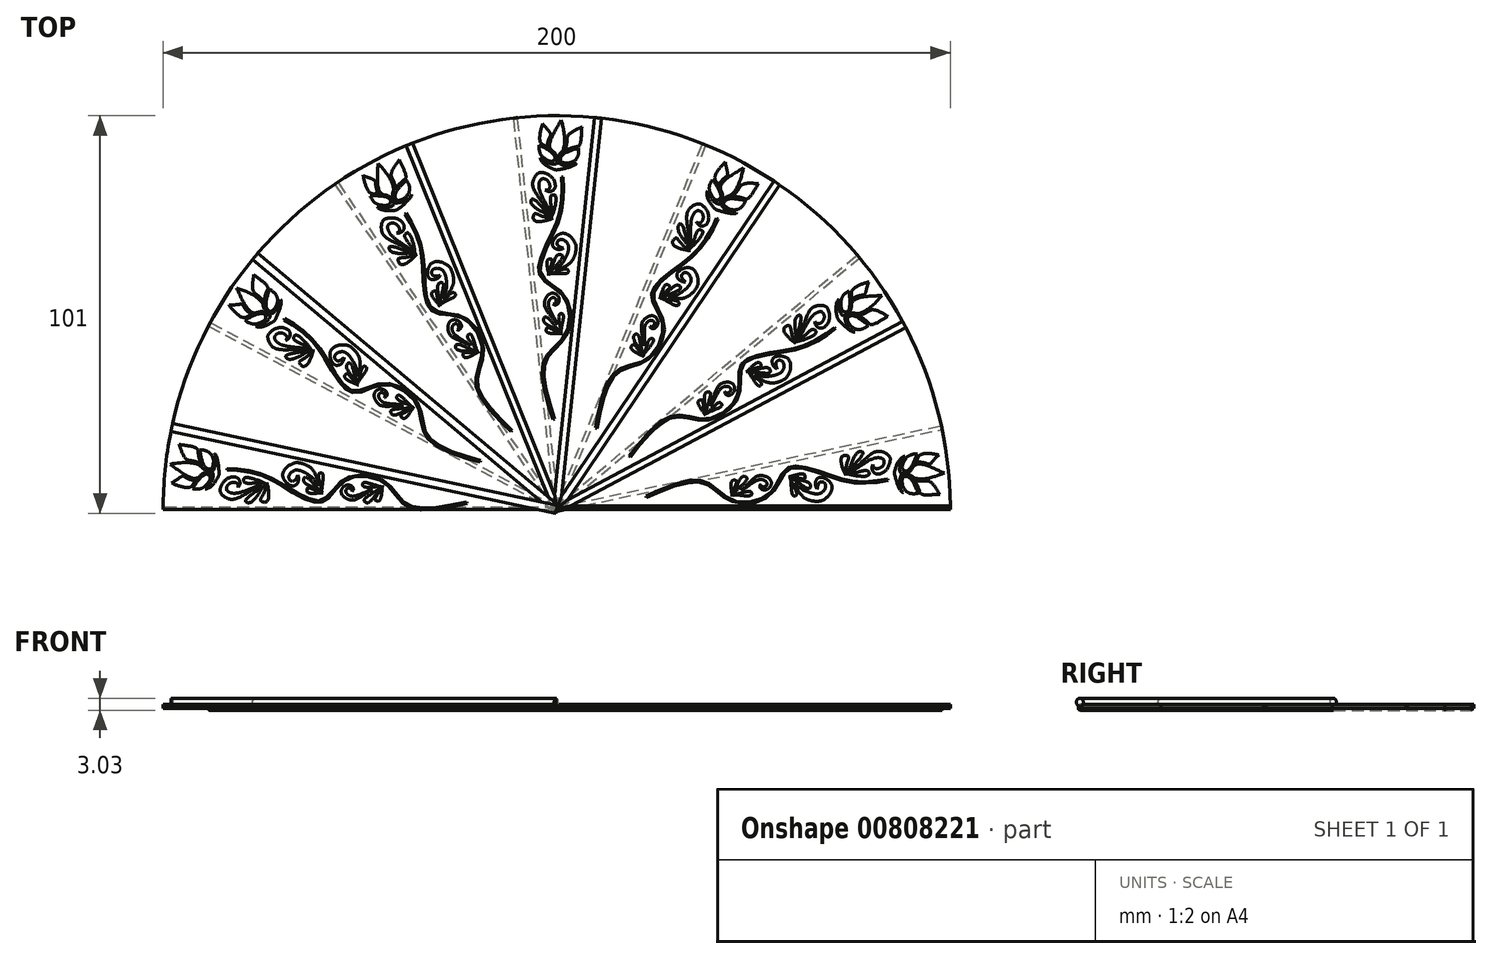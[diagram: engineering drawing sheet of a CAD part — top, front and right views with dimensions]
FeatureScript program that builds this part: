
annotation { "Feature Type Name" : "Feature", "Feature Type Description" : "" }
export const myFeature = defineFeature(function(context is Context, id is Id, definition is map)
    precondition{}
    {
        {
            var Q0;
            Q0=qCreatedBy(makeId("Top.planeOp"),FACE);
            var sketch = newSketch(context, id + "F0", { "sketchPlane" : qUnion([Q0])});
            skLineSegment(sketch, "E0", {"start": v(0, 0) * mm, "end": v(100, 0) * mm});
            skLineSegment(sketch, "E1", {"start": v(0, 0) * mm, "end": v(-100, 0) * mm});
            skArc(sketch, "E2", {"start": v(100, 0) * mm, "mid": v(0, 100) * mm, "end": v(-100, 0) * mm});
            skLineSegment(sketch, "E3.1.0", {"start": v(0, 0) * mm, "end": v(-97.5, 22.25) * mm});
            skLineSegment(sketch, "E3.2.0", {"start": v(0, 0) * mm, "end": v(-90.1, 43.39) * mm});
            skLineSegment(sketch, "E3.3.0", {"start": v(0, 0) * mm, "end": v(-78.18, 62.35) * mm});
            skLineSegment(sketch, "E3.4.0", {"start": v(0, 0) * mm, "end": v(-62.35, 78.18) * mm});
            skLineSegment(sketch, "E3.5.0", {"start": v(0, 0) * mm, "end": v(-43.39, 90.1) * mm});
            skLineSegment(sketch, "E3.6.0", {"start": v(0, 0) * mm, "end": v(-22.25, 97.5) * mm});
            skLineSegment(sketch, "E3.7.0", {"start": v(0, 0) * mm, "end": v(0, 100) * mm});
            skLineSegment(sketch, "E3.8.0", {"start": v(0, 0) * mm, "end": v(22.25, 97.5) * mm});
            skLineSegment(sketch, "E3.9.0", {"start": v(0, 0) * mm, "end": v(43.39, 90.1) * mm});
            skLineSegment(sketch, "E3.10.0", {"start": v(0, 0) * mm, "end": v(62.35, 78.18) * mm});
            skLineSegment(sketch, "E3.11.0", {"start": v(0, 0) * mm, "end": v(78.18, 62.35) * mm});
            skLineSegment(sketch, "E3.12.0", {"start": v(0, 0) * mm, "end": v(90.1, 43.39) * mm});
            skLineSegment(sketch, "E3.13.0", {"start": v(0, 0) * mm, "end": v(97.5, 22.25) * mm});
            skLineSegment(sketch, "E3.anchor1", {"start": v(0, 0) * mm, "end": v(-100, 0) * mm, "construction": true});
            skLineSegment(sketch, "E3.anchor2", {"start": v(0, 0) * mm, "end": v(100, 0) * mm, "construction": true});
            skSolve(sketch);
        }
        {
            var Q0;
            Q0 = qSketchRegion(id + "F0", true);
            extrude(context, id + "F1", {"entities" : qUnion([Q0]), "depth" : 0.5 * mm, "offsetDistance" : 25 * mm, "hasSecondDirection" : true, "secondDirectionOppositeDirection" : true, "secondDirectionDepth" : 0.5 * mm});
        }
        {
            var Q0;
            Q0=qCreatedBy(makeId("Right.planeOp"),FACE);
            var sketch = newSketch(context, id + "F2", { "sketchPlane" : qUnion([Q0])});
            skCircle(sketch, "E4", {"center": v(0, 1.02) * mm, "radius": 1.02 * mm});
            skSolve(sketch);
        }
        {
            var Q0;
            Q0=qCreatedBy(makeId("Right.planeOp"),FACE);
            var sketch = newSketch(context, id + "F3", { "sketchPlane" : qUnion([Q0])});
            skCircle(sketch, "E5", {"center": v(0, -0.5) * mm, "radius": 0.5 * mm});
            skSolve(sketch);
        }
        {
            var Q0;
            Q0=qCreatedBy(makeId("Front.planeOp"),FACE);
            var sketch = newSketch(context, id + "F4", { "sketchPlane" : qUnion([Q0])});
            skLineSegment(sketch, "E6", {"start": v(0, 38.03) * mm, "end": v(0, -33.46) * mm});
            skSolve(sketch);
        }
        {
            var Q0;
            Q0=makeQuery(id+"F2.imprint","IMPRINT",FACE,{"disambiguationData":[TD([[makeQuery(id+"F2.imprint","IMPRINT",EDGE,{"derivedFrom":sQuery(id+"F2.wireOp",EDGE,"E4")}),1.0]])]});
            var Q1;
            Q1=sQuery(id+"F0.wireOp",EDGE,"E0");
            sweep(context, id + "F5", {"profiles" : qUnion([Q0]), "path" : qUnion([Q1])});
        }
        {
            var Q0;
            Q0 = qSketchRegion(id + "F3", true);
            var Q1;
            Q1=sQuery(id+"F0.wireOp",EDGE,"E1");
            sweep(context, id + "F6", {"profiles" : qUnion([Q0]), "path" : qUnion([Q1])});
        }
        {
            var Q0;
            {var subQ0=sQuery(id+"F0.wireOp",EDGE,"E2");var subQ1=sQuery(id+"F0.wireOp",EDGE,"E0");var subQ2=makeQuery(id+"F5.opSweep","SWEPT_FACE",FACE,{"disambiguationData":[OSD([subQ1,sQuery(id+"F2.wireOp",EDGE,"E4")])]});Q0=makeQuery(id+"FwSYZOw7anEKPHd_2.opBoolean","SPLIT",FACE,{"disambiguationData":[TD([makeQuery(id+"F1.opExtrude","SWEPT_FACE",FACE,{"disambiguationData":[OSD([subQ0])]}),subQ2,makeQuery(id+"F9.opPattern","COPY",FACE,{"derivedFrom":subQ2,"instanceName":"1"})])],"derivedFrom":makeQuery(id+"F1.opExtrude","CAP_FACE",FACE,{"disambiguationData":[OSD([sQuery(id+"F0.wireOp",EDGE,"E1"),subQ0,subQ1])],"isStart":false})});}
            var sketch = newSketch(context, id + "F7", { "sketchPlane" : qUnion([Q0])});
            skFitSpline(sketch, "E7", {"points": [v(44.53, 3.26) * mm, v(45.24, 7.41) * mm], "startDerivative": vector(0.11, 3.76) * mm, "endDerivative": vector(4.9, -1.14) * mm});
            skFitSpline(sketch, "E8", {"points": [v(44.53, 3.26) * mm, v(45.24, 7.41) * mm], "startDerivative": vector(1.14, 7.8) * mm, "endDerivative": vector(-3.64, 0.46) * mm});
            skFitSpline(sketch, "E9", {"points": [v(44.88, 3.66) * mm, v(49.56, 4) * mm], "startDerivative": vector(4.69, 0.34) * mm, "endDerivative": vector(-0.4, 3.42) * mm});
            skFitSpline(sketch, "E10", {"points": [v(49.56, 4) * mm, v(44.88, 3.66) * mm], "startDerivative": vector(-0.11, 4.44) * mm, "endDerivative": vector(-4.69, -0.34) * mm});
            skFitSpline(sketch, "E11", {"points": [v(45.08, 4.02) * mm, v(47.68, 8.4) * mm], "startDerivative": vector(1.67, 4.21) * mm, "endDerivative": vector(3.53, -0.8) * mm});
            skFitSpline(sketch, "E12", {"points": [v(45.08, 4.02) * mm, v(47.68, 8.4) * mm], "startDerivative": vector(2.6, 4.38) * mm, "endDerivative": vector(-6.6, 1.37) * mm});
            skFitSpline(sketch, "E13", {"points": [v(46.77, 4.76) * mm, v(52, 8.6) * mm], "startDerivative": vector(5.22, 3.83) * mm, "endDerivative": vector(5.75, -0.34) * mm});
            skFitSpline(sketch, "E14", {"points": [v(52, 8.6) * mm, v(54.53, 6.79) * mm], "startDerivative": vector(2.9, -0.11) * mm, "endDerivative": vector(0.34, -3.59) * mm});
            skFitSpline(sketch, "E15", {"points": [v(54.53, 6.79) * mm, v(52.58, 4.93) * mm], "startDerivative": vector(0.11, -2.9) * mm, "endDerivative": vector(-3.59, 0.34) * mm});
            skFitSpline(sketch, "E16", {"points": [v(52.58, 4.93) * mm, v(51.78, 6.37) * mm], "startDerivative": vector(-2.16, 0.17) * mm, "endDerivative": vector(1.54, 1.88) * mm});
            skFitSpline(sketch, "E17", {"points": [v(46.77, 4.76) * mm, v(51.63, 7.57) * mm], "startDerivative": vector(4.93, 2.5) * mm, "endDerivative": vector(3.64, 0.11) * mm});
            skFitSpline(sketch, "E18", {"points": [v(51.63, 7.57) * mm, v(53.38, 6.7) * mm], "startDerivative": vector(2.62, 0.17) * mm, "endDerivative": vector(0.8, -1.65) * mm});
            skFitSpline(sketch, "E19", {"points": [v(51.78, 6.37) * mm, v(52.83, 5.74) * mm], "startDerivative": vector(0.17, -1.37) * mm, "endDerivative": vector(2.16, 0.57) * mm});
            skFitSpline(sketch, "E20", {"points": [v(52.83, 5.74) * mm, v(53.38, 6.7) * mm], "startDerivative": vector(1.82, 0.23) * mm, "endDerivative": vector(-0.23, 0.85) * mm});
            skFitSpline(sketch, "E21", {"points": [v(58.9, 8.22) * mm, v(63.1, 8.25) * mm], "startDerivative": vector(3.72, 0.54) * mm, "endDerivative": vector(-0.27, -5.02) * mm});
            skFitSpline(sketch, "E22", {"points": [v(58.9, 8.22) * mm, v(63.1, 8.25) * mm], "startDerivative": vector(7.88, 0.23) * mm, "endDerivative": vector(-0.18, 3.67) * mm});
            skFitSpline(sketch, "E23", {"points": [v(59.34, 7.96) * mm, v(60.5, 3.4) * mm], "startDerivative": vector(1.15, -4.56) * mm, "endDerivative": vector(3.3, 0.99) * mm});
            skFitSpline(sketch, "E24", {"points": [v(60.5, 3.4) * mm, v(59.34, 7.96) * mm], "startDerivative": vector(4.35, 0.88) * mm, "endDerivative": vector(-1.15, 4.56) * mm});
            skFitSpline(sketch, "E25", {"points": [v(59.73, 7.81) * mm, v(64.5, 6.01) * mm], "startDerivative": vector(4.44, -0.91) * mm, "endDerivative": vector(-0.17, -3.61) * mm});
            skFitSpline(sketch, "E26", {"points": [v(59.73, 7.81) * mm, v(64.5, 6.01) * mm], "startDerivative": vector(4.77, -1.8) * mm, "endDerivative": vector(0.2, 6.74) * mm});
            skFitSpline(sketch, "E27", {"points": [v(60.56, 6.79) * mm, v(63.6, 2.55) * mm], "startDerivative": vector(1.76, -6.57) * mm, "endDerivative": vector(4.13, -1.83) * mm});
            skFitSpline(sketch, "E28", {"points": [v(63.6, 2.55) * mm, v(67.96, 2.55) * mm], "startDerivative": vector(2.64, -1.35) * mm, "endDerivative": vector(2.98, 2.7) * mm});
            skFitSpline(sketch, "E29", {"points": [v(67.96, 2.55) * mm, v(69.74, 6.4) * mm], "startDerivative": vector(3.66, 2.1) * mm, "endDerivative": vector(-2.1, 4.06) * mm});
            skFitSpline(sketch, "E30", {"points": [v(69.74, 6.4) * mm, v(66.9, 8.14) * mm], "startDerivative": vector(-1.08, 2.44) * mm, "endDerivative": vector(-3.18, -0.34) * mm});
            skFitSpline(sketch, "E31", {"points": [v(66.9, 8.14) * mm, v(66.18, 5.19) * mm], "startDerivative": vector(-3.52, -0.34) * mm, "endDerivative": vector(2.64, -3.11) * mm});
            skFitSpline(sketch, "E32", {"points": [v(66.18, 5.19) * mm, v(67.33, 7) * mm], "startDerivative": vector(0.6, 3.59) * mm, "endDerivative": vector(2.16, 0) * mm});
            skFitSpline(sketch, "E33", {"points": [v(67.33, 7) * mm, v(67.49, 4.33) * mm], "startDerivative": vector(3.18, 0) * mm, "endDerivative": vector(-4, -3.52) * mm});
            skFitSpline(sketch, "E34", {"points": [v(67.49, 4.33) * mm, v(64.08, 4.33) * mm], "startDerivative": vector(-2.98, -2.17) * mm, "endDerivative": vector(-3.05, 1.02) * mm});
            skFitSpline(sketch, "E35", {"points": [v(64.08, 4.33) * mm, v(60.56, 6.79) * mm], "startDerivative": vector(-2.17, 0.88) * mm, "endDerivative": vector(-5.08, 6.23) * mm});
            skFitSpline(sketch, "E36", {"points": [v(73.49, 8.63) * mm, v(73.45, 13.69) * mm], "startDerivative": vector(-2.81, 4.93) * mm, "endDerivative": vector(6.77, -0.81) * mm});
            skFitSpline(sketch, "E37", {"points": [v(73.49, 8.63) * mm, v(73.45, 13.69) * mm], "startDerivative": vector(-1.19, 10.9) * mm, "endDerivative": vector(-5.28, 0.47) * mm});
            skFitSpline(sketch, "E38", {"points": [v(73.83, 9.03) * mm, v(79.39, 9.06) * mm], "startDerivative": vector(5.17, -1.75) * mm, "endDerivative": vector(-0.4, 3.42) * mm});
            skFitSpline(sketch, "E39", {"points": [v(79.39, 9.06) * mm, v(73.83, 9.03) * mm], "startDerivative": vector(-0.4, 5.62) * mm, "endDerivative": vector(-8.48, 0.05) * mm});
            skFitSpline(sketch, "E40", {"points": [v(74.04, 9.4) * mm, v(77.58, 14.63) * mm], "startDerivative": vector(1.67, 4.21) * mm, "endDerivative": vector(5.69, -2.03) * mm});
            skFitSpline(sketch, "E41", {"points": [v(74.04, 9.4) * mm, v(77.58, 14.63) * mm], "startDerivative": vector(2.6, 4.38) * mm, "endDerivative": vector(-3.45, 1.35) * mm});
            skFitSpline(sketch, "E42", {"points": [v(74.72, 9.51) * mm, v(81.24, 14.7) * mm], "startDerivative": vector(5.22, 3.83) * mm, "endDerivative": vector(5.96, 1.35) * mm});
            skFitSpline(sketch, "E43", {"points": [v(81.24, 14.7) * mm, v(84.73, 12.87) * mm], "startDerivative": vector(4, 0.88) * mm, "endDerivative": vector(0.34, -3.59) * mm});
            skFitSpline(sketch, "E44", {"points": [v(84.73, 12.87) * mm, v(81.78, 8.95) * mm], "startDerivative": vector(0.11, -2.9) * mm, "endDerivative": vector(-7.18, -1.06) * mm});
            skFitSpline(sketch, "E45", {"points": [v(81.78, 8.95) * mm, v(80.33, 11.38) * mm], "startDerivative": vector(-2.5, -0.6) * mm, "endDerivative": vector(2.57, 4.74) * mm});
            skFitSpline(sketch, "E46", {"points": [v(74.72, 9.51) * mm, v(80.58, 12.94) * mm], "startDerivative": vector(4.93, 2.5) * mm, "endDerivative": vector(4.2, 0.95) * mm});
            skFitSpline(sketch, "E47", {"points": [v(80.58, 12.94) * mm, v(83.1, 12.44) * mm], "startDerivative": vector(2.98, 1.02) * mm, "endDerivative": vector(0.55, -2.11) * mm});
            skFitSpline(sketch, "E48", {"points": [v(80.33, 11.38) * mm, v(82, 10.46) * mm], "startDerivative": vector(-0.1, -2.43) * mm, "endDerivative": vector(3.11, 1.29) * mm});
            skFitSpline(sketch, "E49", {"points": [v(82, 10.46) * mm, v(83.1, 12.44) * mm], "startDerivative": vector(3.62, 1.47) * mm, "endDerivative": vector(-0.54, 1.43) * mm});
            skFitSpline(sketch, "E50", {"points": [v(85.76, 9.2) * mm, v(88.02, 4.26) * mm], "startDerivative": vector(-0.03, -1.21) * mm, "endDerivative": vector(2.65, 0.5) * mm});
            skFitSpline(sketch, "E51", {"points": [v(85.76, 9.2) * mm, v(88.48, 13.54) * mm], "startDerivative": vector(-0.05, 1.44) * mm, "endDerivative": vector(5.54, 1.43) * mm});
            skFitSpline(sketch, "E52", {"points": [v(88.02, 4.26) * mm, v(87.68, 8.94) * mm], "startDerivative": vector(-3.48, 2.68) * mm, "endDerivative": vector(2.23, 2.48) * mm});
            skFitSpline(sketch, "E53", {"points": [v(87.68, 8.94) * mm, v(88.48, 13.54) * mm], "startDerivative": vector(-4.06, 2.42) * mm, "endDerivative": vector(2.25, 2.17) * mm});
            skFitSpline(sketch, "E54", {"points": [v(88.11, 8.27) * mm, v(88, 5.68) * mm], "startDerivative": vector(-1.59, -0.52) * mm, "endDerivative": vector(0.92, -2.03) * mm});
            skFitSpline(sketch, "E55", {"points": [v(88, 5.68) * mm, v(91.86, 4.1) * mm], "startDerivative": vector(2.15, -4.56) * mm, "endDerivative": vector(5.99, 1.24) * mm});
            skFitSpline(sketch, "E56", {"points": [v(91.86, 4.1) * mm, v(88.11, 8.27) * mm], "startDerivative": vector(-3.25, 7.52) * mm, "endDerivative": vector(-5.34, -1.96) * mm});
            skFitSpline(sketch, "E57", {"points": [v(88.48, 12.56) * mm, v(87.86, 10.28) * mm], "startDerivative": vector(-1.02, -1.74) * mm, "endDerivative": vector(0.98, -2.03) * mm});
            skFitSpline(sketch, "E58", {"points": [v(87.86, 10.28) * mm, v(91.58, 14.08) * mm], "startDerivative": vector(4.26, -6.22) * mm, "endDerivative": vector(1.68, 5.02) * mm});
            skFitSpline(sketch, "E59", {"points": [v(91.58, 14.08) * mm, v(88.48, 12.56) * mm], "startDerivative": vector(-6.26, -0.07) * mm, "endDerivative": vector(-1.28, -2.1) * mm});
            skFitSpline(sketch, "E60", {"points": [v(87.77, 9.48) * mm, v(88, 8.58) * mm], "startDerivative": vector(1.48, -1.3) * mm, "endDerivative": vector(-0.53, -0.75) * mm});
            skFitSpline(sketch, "E61", {"points": [v(88, 8.58) * mm, v(90.13, 8.5) * mm], "startDerivative": vector(1.18, 0.66) * mm, "endDerivative": vector(1.77, -1.63) * mm});
            skFitSpline(sketch, "E62", {"points": [v(90.13, 8.5) * mm, v(98.44, 9.22) * mm], "startDerivative": vector(4.45, -4.98) * mm, "endDerivative": vector(6.68, 3.1) * mm});
            skFitSpline(sketch, "E63", {"points": [v(90.67, 7.56) * mm, v(92.22, 4.32) * mm], "startDerivative": vector(2.32, -2.66) * mm, "endDerivative": vector(0.49, -2.76) * mm});
            skFitSpline(sketch, "E64", {"points": [v(90.67, 7.56) * mm, v(94, 7.26) * mm], "startDerivative": vector(2.63, -1.3) * mm, "endDerivative": vector(2.03, 0.38) * mm});
            skFitSpline(sketch, "E65", {"points": [v(94, 7.26) * mm, v(97.32, 3.78) * mm], "startDerivative": vector(4.8, -0.09) * mm, "endDerivative": vector(2.12, -2.72) * mm});
            skFitSpline(sketch, "E66", {"points": [v(97.32, 3.78) * mm, v(92.22, 4.32) * mm], "startDerivative": vector(-3.5, 0.44) * mm, "endDerivative": vector(-1.19, 3.52) * mm});
            skFitSpline(sketch, "E67", {"points": [v(91.2, 11.93) * mm, v(94.43, 11.46) * mm], "startDerivative": vector(3.66, 0.77) * mm, "endDerivative": vector(1.33, -0.8) * mm});
            skFitSpline(sketch, "E68", {"points": [v(97.13, 13.78) * mm, v(94.43, 11.46) * mm], "startDerivative": vector(-2.65, -1.5) * mm, "endDerivative": vector(-1.94, 0.46) * mm});
            skFitSpline(sketch, "E69", {"points": [v(91.2, 11.93) * mm, v(92.03, 13.6) * mm], "startDerivative": vector(1.13, 1.22) * mm, "endDerivative": vector(0.97, 0.97) * mm});
            skFitSpline(sketch, "E70", {"points": [v(97.13, 13.78) * mm, v(92.03, 13.6) * mm], "startDerivative": vector(-2.57, 0.88) * mm, "endDerivative": vector(-2.34, -3.05) * mm});
            skFitSpline(sketch, "E71", {"points": [v(98.44, 9.22) * mm, v(90.67, 10.97) * mm], "startDerivative": vector(-7.55, 3) * mm, "endDerivative": vector(-4.76, -4.68) * mm});
            skFitSpline(sketch, "E72", {"points": [v(90.67, 10.97) * mm, v(87.77, 9.48) * mm], "startDerivative": vector(-3.68, -6.25) * mm, "endDerivative": vector(-2.93, 0.69) * mm});
            skFitSpline(sketch, "E73", {"points": [v(22.78, 2.98) * mm, v(37.2, 6.72) * mm, v(44.15, 2.16) * mm, v(54.32, 3.74) * mm, v(59.25, 10.33) * mm, v(72.74, 7.24) * mm, v(84.11, 7.27) * mm], "startDerivative": vector(84.34, 36.8) * mm, "endDerivative": vector(62.25, 9.7) * mm});
            skFitSpline(sketch, "E74.0", {"points": [v(22.62, 3.35) * mm, v(24.38, 4.11) * mm, v(27.02, 5.27) * mm, v(30.37, 6.47) * mm, v(32.75, 7.12) * mm, v(34.6, 7.38) * mm, v(35.97, 7.36) * mm, v(36.94, 7.23) * mm, v(37.85, 6.95) * mm, v(38.67, 6.55) * mm, v(39.44, 6.06) * mm, v(40.4, 5.33) * mm, v(41.53, 4.33) * mm, v(42.7, 3.4) * mm, v(43.74, 2.78) * mm, v(44.85, 2.28) * mm, v(46.45, 1.9) * mm, v(48.55, 1.83) * mm, v(50.63, 2.16) * mm, v(52.23, 2.76) * mm, v(53.34, 3.43) * mm, v(54.07, 4.03) * mm, v(54.69, 4.72) * mm, v(55.4, 5.75) * mm, v(56.17, 7.16) * mm, v(56.9, 8.55) * mm, v(57.58, 9.53) * mm, v(58.18, 10.16) * mm, v(58.78, 10.57) * mm, v(59.34, 10.8) * mm, v(59.93, 10.95) * mm, v(60.72, 11.03) * mm, v(61.74, 10.97) * mm, v(62.83, 10.79) * mm, v(64.36, 10.4) * mm, v(66.4, 9.75) * mm, v(68.51, 8.99) * mm, v(70.2, 8.4) * mm, v(71.44, 8) * mm, v(72.65, 7.66) * mm, v(73.82, 7.4) * mm, v(74.94, 7.21) * mm, v(76.4, 7.05) * mm, v(78.14, 7) * mm, v(80.15, 7.12) * mm, v(82.1, 7.36) * mm, v(83.4, 7.56) * mm, v(84.05, 7.66) * mm]});
            skLineSegment(sketch, "E75", {"start": v(84.11, 7.27) * mm, "end": v(84.05, 7.66) * mm});
            skLineSegment(sketch, "E76", {"start": v(22.62, 3.35) * mm, "end": v(22.78, 2.98) * mm});
            skSolve(sketch);
        }
        {
            var Q0;
            Q0 = qSketchRegion(id + "F7", true);
            extrude(context, id + "F8", {"entities" : qUnion([Q0]), "oppositeDirection" : true, "depth" : 0.4 * mm, "offsetDistance" : 25 * mm});
        }
        {
            var Q0;
            Q0=makeQuery(id+"F5.opSweep","SWEPT_BODY",BODY,{"disambiguationData":[OSD([sQuery(id+"F0.wireOp",EDGE,"E3.7.0"),sQuery(id+"F2.wireOp",EDGE,"E4")])]});
            var Q1;
            Q1=makeQuery(id+"F8.opExtrude","SWEPT_BODY",BODY,{"disambiguationData":[OSD([sQuery(id+"F7.wireOp",EDGE,"E63"),sQuery(id+"F7.wireOp",EDGE,"E64"),sQuery(id+"F7.wireOp",EDGE,"E65"),sQuery(id+"F7.wireOp",EDGE,"E66")])]});
            var Q2;
            Q2=makeQuery(id+"F8.opExtrude","SWEPT_BODY",BODY,{"disambiguationData":[OSD([sQuery(id+"F7.wireOp",EDGE,"E54"),sQuery(id+"F7.wireOp",EDGE,"E55"),sQuery(id+"F7.wireOp",EDGE,"E56")])]});
            var Q3;
            Q3=makeQuery(id+"F8.opExtrude","SWEPT_BODY",BODY,{"disambiguationData":[OSD([sQuery(id+"F7.wireOp",EDGE,"E42"),sQuery(id+"F7.wireOp",EDGE,"E43"),sQuery(id+"F7.wireOp",EDGE,"E44"),sQuery(id+"F7.wireOp",EDGE,"E45"),sQuery(id+"F7.wireOp",EDGE,"E46"),sQuery(id+"F7.wireOp",EDGE,"E47"),sQuery(id+"F7.wireOp",EDGE,"E48"),sQuery(id+"F7.wireOp",EDGE,"E49")])]});
            var Q4;
            Q4=makeQuery(id+"F8.opExtrude","SWEPT_BODY",BODY,{"disambiguationData":[OSD([sQuery(id+"F7.wireOp",EDGE,"E40"),sQuery(id+"F7.wireOp",EDGE,"E41")])]});
            var Q5;
            Q5=makeQuery(id+"F8.opExtrude","SWEPT_BODY",BODY,{"disambiguationData":[OSD([sQuery(id+"F7.wireOp",EDGE,"E36"),sQuery(id+"F7.wireOp",EDGE,"E37")])]});
            var Q6;
            Q6=makeQuery(id+"F8.opExtrude","SWEPT_BODY",BODY,{"disambiguationData":[OSD([sQuery(id+"F7.wireOp",EDGE,"E38"),sQuery(id+"F7.wireOp",EDGE,"E39")])]});
            var Q7;
            Q7=makeQuery(id+"F8.opExtrude","SWEPT_BODY",BODY,{"disambiguationData":[OSD([sQuery(id+"F7.wireOp",EDGE,"E73"),sQuery(id+"F7.wireOp",EDGE,"E74.0"),sQuery(id+"F7.wireOp",EDGE,"E75"),sQuery(id+"F7.wireOp",EDGE,"E76")])]});
            var Q8;
            Q8=makeQuery(id+"F8.opExtrude","SWEPT_BODY",BODY,{"disambiguationData":[OSD([sQuery(id+"F7.wireOp",EDGE,"E67"),sQuery(id+"F7.wireOp",EDGE,"E68"),sQuery(id+"F7.wireOp",EDGE,"E69"),sQuery(id+"F7.wireOp",EDGE,"E70")])]});
            var Q9;
            Q9=makeQuery(id+"F8.opExtrude","SWEPT_BODY",BODY,{"disambiguationData":[OSD([sQuery(id+"F7.wireOp",EDGE,"E60"),sQuery(id+"F7.wireOp",EDGE,"E61"),sQuery(id+"F7.wireOp",EDGE,"E62"),sQuery(id+"F7.wireOp",EDGE,"E71"),sQuery(id+"F7.wireOp",EDGE,"E72")])]});
            var Q10;
            Q10=makeQuery(id+"F8.opExtrude","SWEPT_BODY",BODY,{"disambiguationData":[OSD([sQuery(id+"F7.wireOp",EDGE,"E50"),sQuery(id+"F7.wireOp",EDGE,"E51"),sQuery(id+"F7.wireOp",EDGE,"E52"),sQuery(id+"F7.wireOp",EDGE,"E53")])]});
            var Q11;
            Q11=makeQuery(id+"F8.opExtrude","SWEPT_BODY",BODY,{"disambiguationData":[OSD([sQuery(id+"F7.wireOp",EDGE,"E57"),sQuery(id+"F7.wireOp",EDGE,"E58"),sQuery(id+"F7.wireOp",EDGE,"E59")])]});
            var Q12;
            Q12=makeQuery(id+"F8.opExtrude","SWEPT_BODY",BODY,{"disambiguationData":[OSD([sQuery(id+"F7.wireOp",EDGE,"E27"),sQuery(id+"F7.wireOp",EDGE,"E28"),sQuery(id+"F7.wireOp",EDGE,"E29"),sQuery(id+"F7.wireOp",EDGE,"E30"),sQuery(id+"F7.wireOp",EDGE,"E31"),sQuery(id+"F7.wireOp",EDGE,"E32"),sQuery(id+"F7.wireOp",EDGE,"E33"),sQuery(id+"F7.wireOp",EDGE,"E34"),sQuery(id+"F7.wireOp",EDGE,"E35")])]});
            var Q13;
            Q13=makeQuery(id+"F8.opExtrude","SWEPT_BODY",BODY,{"disambiguationData":[OSD([sQuery(id+"F7.wireOp",EDGE,"E21"),sQuery(id+"F7.wireOp",EDGE,"E22")])]});
            var Q14;
            Q14=makeQuery(id+"F8.opExtrude","SWEPT_BODY",BODY,{"disambiguationData":[OSD([sQuery(id+"F7.wireOp",EDGE,"E25"),sQuery(id+"F7.wireOp",EDGE,"E26")])]});
            var Q15;
            Q15=makeQuery(id+"F8.opExtrude","SWEPT_BODY",BODY,{"disambiguationData":[OSD([sQuery(id+"F7.wireOp",EDGE,"E23"),sQuery(id+"F7.wireOp",EDGE,"E24")])]});
            var Q16;
            Q16=makeQuery(id+"F8.opExtrude","SWEPT_BODY",BODY,{"disambiguationData":[OSD([sQuery(id+"F7.wireOp",EDGE,"E13"),sQuery(id+"F7.wireOp",EDGE,"E14"),sQuery(id+"F7.wireOp",EDGE,"E15"),sQuery(id+"F7.wireOp",EDGE,"E16"),sQuery(id+"F7.wireOp",EDGE,"E17"),sQuery(id+"F7.wireOp",EDGE,"E18"),sQuery(id+"F7.wireOp",EDGE,"E19"),sQuery(id+"F7.wireOp",EDGE,"E20")])]});
            var Q17;
            Q17=makeQuery(id+"F8.opExtrude","SWEPT_BODY",BODY,{"disambiguationData":[OSD([sQuery(id+"F7.wireOp",EDGE,"E11"),sQuery(id+"F7.wireOp",EDGE,"E12")])]});
            var Q18;
            Q18=makeQuery(id+"F8.opExtrude","SWEPT_BODY",BODY,{"disambiguationData":[OSD([sQuery(id+"F7.wireOp",EDGE,"E7"),sQuery(id+"F7.wireOp",EDGE,"E8")])]});
            var Q19;
            Q19=makeQuery(id+"F8.opExtrude","SWEPT_BODY",BODY,{"disambiguationData":[OSD([sQuery(id+"F7.wireOp",EDGE,"E9"),sQuery(id+"F7.wireOp",EDGE,"E10")])]});
            var Q20;
            Q20=sQuery(id+"F4.wireOp",EDGE,"E6");
            circularPattern(context, id + "F9", {"entities" : qUnion([Q0, Q1, Q2, Q3, Q4, Q5, Q6, Q7, Q8, Q9, Q10, Q11, Q12, Q13, Q14, Q15, Q16, Q17, Q18, Q19]), "axis" : qUnion([Q20]), "angle" : 168 * degree, "instanceCount" : 7, "oppositeDirection" : true, "equalSpace" : true});
        }
        {
            var Q0;
            Q0=makeQuery(id+"F6.opSweep","SWEPT_BODY",BODY,{"disambiguationData":[OSD([sQuery(id+"F0.wireOp",EDGE,"E1"),sQuery(id+"F3.wireOp",EDGE,"E5")])]});
            var Q1;
            Q1=sQuery(id+"F4.wireOp",EDGE,"E6");
            circularPattern(context, id + "F10", {"entities" : qUnion([Q0]), "axis" : qUnion([Q1]), "angle" : 168 * degree, "instanceCount" : 7, "equalSpace" : true});
        }
        {
            var Q0;
            Q0=makeQuery(id+"F5.opSweep","SWEPT_BODY",BODY,{"disambiguationData":[OSD([sQuery(id+"F0.wireOp",EDGE,"E0"),sQuery(id+"F2.wireOp",EDGE,"E4")])]});
            var Q1;
            Q1=makeQuery(id+"F6.opSweep","SWEPT_BODY",BODY,{"disambiguationData":[OSD([sQuery(id+"F0.wireOp",EDGE,"E1"),sQuery(id+"F3.wireOp",EDGE,"E5")])]});
            var Q2;
            Q2=makeQuery(id+"F8.opExtrude","SWEPT_BODY",BODY,{"disambiguationData":[OSD([sQuery(id+"F7.wireOp",EDGE,"E7"),sQuery(id+"F7.wireOp",EDGE,"E8")])]});
            var Q3;
            Q3=makeQuery(id+"F8.opExtrude","SWEPT_BODY",BODY,{"disambiguationData":[OSD([sQuery(id+"F7.wireOp",EDGE,"E9"),sQuery(id+"F7.wireOp",EDGE,"E10")])]});
            var Q4;
            Q4=makeQuery(id+"F8.opExtrude","SWEPT_BODY",BODY,{"disambiguationData":[OSD([sQuery(id+"F7.wireOp",EDGE,"E11"),sQuery(id+"F7.wireOp",EDGE,"E12")])]});
            var Q5;
            Q5=makeQuery(id+"F8.opExtrude","SWEPT_BODY",BODY,{"disambiguationData":[OSD([sQuery(id+"F7.wireOp",EDGE,"E13"),sQuery(id+"F7.wireOp",EDGE,"E14"),sQuery(id+"F7.wireOp",EDGE,"E15"),sQuery(id+"F7.wireOp",EDGE,"E16"),sQuery(id+"F7.wireOp",EDGE,"E17"),sQuery(id+"F7.wireOp",EDGE,"E18"),sQuery(id+"F7.wireOp",EDGE,"E19"),sQuery(id+"F7.wireOp",EDGE,"E20")])]});
            var Q6;
            Q6=makeQuery(id+"F8.opExtrude","SWEPT_BODY",BODY,{"disambiguationData":[OSD([sQuery(id+"F7.wireOp",EDGE,"E21"),sQuery(id+"F7.wireOp",EDGE,"E22")])]});
            var Q7;
            Q7=makeQuery(id+"F8.opExtrude","SWEPT_BODY",BODY,{"disambiguationData":[OSD([sQuery(id+"F7.wireOp",EDGE,"E23"),sQuery(id+"F7.wireOp",EDGE,"E24")])]});
            var Q8;
            Q8=makeQuery(id+"F8.opExtrude","SWEPT_BODY",BODY,{"disambiguationData":[OSD([sQuery(id+"F7.wireOp",EDGE,"E27"),sQuery(id+"F7.wireOp",EDGE,"E28"),sQuery(id+"F7.wireOp",EDGE,"E29"),sQuery(id+"F7.wireOp",EDGE,"E30"),sQuery(id+"F7.wireOp",EDGE,"E31"),sQuery(id+"F7.wireOp",EDGE,"E32"),sQuery(id+"F7.wireOp",EDGE,"E33"),sQuery(id+"F7.wireOp",EDGE,"E34"),sQuery(id+"F7.wireOp",EDGE,"E35")])]});
            var Q9;
            Q9=makeQuery(id+"F8.opExtrude","SWEPT_BODY",BODY,{"disambiguationData":[OSD([sQuery(id+"F7.wireOp",EDGE,"E25"),sQuery(id+"F7.wireOp",EDGE,"E26")])]});
            var Q10;
            Q10=makeQuery(id+"F8.opExtrude","SWEPT_BODY",BODY,{"disambiguationData":[OSD([sQuery(id+"F7.wireOp",EDGE,"E50"),sQuery(id+"F7.wireOp",EDGE,"E51"),sQuery(id+"F7.wireOp",EDGE,"E52"),sQuery(id+"F7.wireOp",EDGE,"E53")])]});
            var Q11;
            Q11=makeQuery(id+"F8.opExtrude","SWEPT_BODY",BODY,{"disambiguationData":[OSD([sQuery(id+"F7.wireOp",EDGE,"E73"),sQuery(id+"F7.wireOp",EDGE,"E74.0"),sQuery(id+"F7.wireOp",EDGE,"E75"),sQuery(id+"F7.wireOp",EDGE,"E76")])]});
            var Q12;
            Q12=makeQuery(id+"F8.opExtrude","SWEPT_BODY",BODY,{"disambiguationData":[OSD([sQuery(id+"F7.wireOp",EDGE,"E40"),sQuery(id+"F7.wireOp",EDGE,"E41")])]});
            var Q13;
            Q13=makeQuery(id+"F8.opExtrude","SWEPT_BODY",BODY,{"disambiguationData":[OSD([sQuery(id+"F7.wireOp",EDGE,"E36"),sQuery(id+"F7.wireOp",EDGE,"E37")])]});
            var Q14;
            Q14=makeQuery(id+"F8.opExtrude","SWEPT_BODY",BODY,{"disambiguationData":[OSD([sQuery(id+"F7.wireOp",EDGE,"E27"),sQuery(id+"F7.wireOp",EDGE,"E28"),sQuery(id+"F7.wireOp",EDGE,"E29"),sQuery(id+"F7.wireOp",EDGE,"E30"),sQuery(id+"F7.wireOp",EDGE,"E31"),sQuery(id+"F7.wireOp",EDGE,"E32"),sQuery(id+"F7.wireOp",EDGE,"E33"),sQuery(id+"F7.wireOp",EDGE,"E34"),sQuery(id+"F7.wireOp",EDGE,"E35")])]});
            var Q15;
            Q15=makeQuery(id+"F8.opExtrude","SWEPT_BODY",BODY,{"disambiguationData":[OSD([sQuery(id+"F7.wireOp",EDGE,"E67"),sQuery(id+"F7.wireOp",EDGE,"E68"),sQuery(id+"F7.wireOp",EDGE,"E69"),sQuery(id+"F7.wireOp",EDGE,"E70")])]});
            var Q16;
            Q16=makeQuery(id+"F8.opExtrude","SWEPT_BODY",BODY,{"disambiguationData":[OSD([sQuery(id+"F7.wireOp",EDGE,"E63"),sQuery(id+"F7.wireOp",EDGE,"E64"),sQuery(id+"F7.wireOp",EDGE,"E65"),sQuery(id+"F7.wireOp",EDGE,"E66")])]});
            var Q17;
            Q17=makeQuery(id+"F8.opExtrude","SWEPT_BODY",BODY,{"disambiguationData":[OSD([sQuery(id+"F7.wireOp",EDGE,"E60"),sQuery(id+"F7.wireOp",EDGE,"E61"),sQuery(id+"F7.wireOp",EDGE,"E62"),sQuery(id+"F7.wireOp",EDGE,"E71"),sQuery(id+"F7.wireOp",EDGE,"E72")])]});
            var Q18;
            Q18=makeQuery(id+"F8.opExtrude","SWEPT_BODY",BODY,{"disambiguationData":[OSD([sQuery(id+"F7.wireOp",EDGE,"E57"),sQuery(id+"F7.wireOp",EDGE,"E58"),sQuery(id+"F7.wireOp",EDGE,"E59")])]});
            var Q19;
            Q19=makeQuery(id+"F8.opExtrude","SWEPT_BODY",BODY,{"disambiguationData":[OSD([sQuery(id+"F7.wireOp",EDGE,"E38"),sQuery(id+"F7.wireOp",EDGE,"E39")])]});
            var Q20;
            Q20=makeQuery(id+"F8.opExtrude","SWEPT_BODY",BODY,{"disambiguationData":[OSD([sQuery(id+"F7.wireOp",EDGE,"E42"),sQuery(id+"F7.wireOp",EDGE,"E43"),sQuery(id+"F7.wireOp",EDGE,"E44"),sQuery(id+"F7.wireOp",EDGE,"E45"),sQuery(id+"F7.wireOp",EDGE,"E46"),sQuery(id+"F7.wireOp",EDGE,"E47"),sQuery(id+"F7.wireOp",EDGE,"E48"),sQuery(id+"F7.wireOp",EDGE,"E49")])]});
            var Q21;
            Q21=makeQuery(id+"F8.opExtrude","SWEPT_BODY",BODY,{"disambiguationData":[OSD([sQuery(id+"F7.wireOp",EDGE,"E54"),sQuery(id+"F7.wireOp",EDGE,"E55"),sQuery(id+"F7.wireOp",EDGE,"E56")])]});
            var Q22;
            Q22=makeQuery(id+"F9.opPattern","COPY",BODY,{"derivedFrom":makeQuery(id+"F5.opSweep","SWEPT_BODY",BODY,{"disambiguationData":[OSD([sQuery(id+"F0.wireOp",EDGE,"E0"),sQuery(id+"F2.wireOp",EDGE,"E4")])]}),"instanceName":"1"});
            var Q23;
            Q23=makeQuery(id+"F9.opPattern","COPY",BODY,{"derivedFrom":makeQuery(id+"F8.opExtrude","SWEPT_BODY",BODY,{"disambiguationData":[OSD([sQuery(id+"F7.wireOp",EDGE,"E11"),sQuery(id+"F7.wireOp",EDGE,"E12")])]}),"instanceName":"1"});
            var Q24;
            Q24=makeQuery(id+"F9.opPattern","COPY",BODY,{"derivedFrom":makeQuery(id+"F8.opExtrude","SWEPT_BODY",BODY,{"disambiguationData":[OSD([sQuery(id+"F7.wireOp",EDGE,"E13"),sQuery(id+"F7.wireOp",EDGE,"E14"),sQuery(id+"F7.wireOp",EDGE,"E15"),sQuery(id+"F7.wireOp",EDGE,"E16"),sQuery(id+"F7.wireOp",EDGE,"E17"),sQuery(id+"F7.wireOp",EDGE,"E18"),sQuery(id+"F7.wireOp",EDGE,"E19"),sQuery(id+"F7.wireOp",EDGE,"E20")])]}),"instanceName":"1"});
            var Q25;
            Q25=makeQuery(id+"F9.opPattern","COPY",BODY,{"derivedFrom":makeQuery(id+"F8.opExtrude","SWEPT_BODY",BODY,{"disambiguationData":[OSD([sQuery(id+"F7.wireOp",EDGE,"E23"),sQuery(id+"F7.wireOp",EDGE,"E24")])]}),"instanceName":"1"});
            var Q26;
            Q26=makeQuery(id+"F9.opPattern","COPY",BODY,{"derivedFrom":makeQuery(id+"F8.opExtrude","SWEPT_BODY",BODY,{"disambiguationData":[OSD([sQuery(id+"F7.wireOp",EDGE,"E25"),sQuery(id+"F7.wireOp",EDGE,"E26")])]}),"instanceName":"1"});
            var Q27;
            Q27=makeQuery(id+"F9.opPattern","COPY",BODY,{"derivedFrom":makeQuery(id+"F8.opExtrude","SWEPT_BODY",BODY,{"disambiguationData":[OSD([sQuery(id+"F7.wireOp",EDGE,"E38"),sQuery(id+"F7.wireOp",EDGE,"E39")])]}),"instanceName":"1"});
            var Q28;
            Q28=makeQuery(id+"F9.opPattern","COPY",BODY,{"derivedFrom":makeQuery(id+"F8.opExtrude","SWEPT_BODY",BODY,{"disambiguationData":[OSD([sQuery(id+"F7.wireOp",EDGE,"E40"),sQuery(id+"F7.wireOp",EDGE,"E41")])]}),"instanceName":"1"});
            var Q29;
            Q29=makeQuery(id+"F9.opPattern","COPY",BODY,{"derivedFrom":makeQuery(id+"F8.opExtrude","SWEPT_BODY",BODY,{"disambiguationData":[OSD([sQuery(id+"F7.wireOp",EDGE,"E42"),sQuery(id+"F7.wireOp",EDGE,"E43"),sQuery(id+"F7.wireOp",EDGE,"E44"),sQuery(id+"F7.wireOp",EDGE,"E45"),sQuery(id+"F7.wireOp",EDGE,"E46"),sQuery(id+"F7.wireOp",EDGE,"E47"),sQuery(id+"F7.wireOp",EDGE,"E48"),sQuery(id+"F7.wireOp",EDGE,"E49")])]}),"instanceName":"1"});
            var Q30;
            Q30=makeQuery(id+"F9.opPattern","COPY",BODY,{"derivedFrom":makeQuery(id+"F8.opExtrude","SWEPT_BODY",BODY,{"disambiguationData":[OSD([sQuery(id+"F7.wireOp",EDGE,"E7"),sQuery(id+"F7.wireOp",EDGE,"E8")])]}),"instanceName":"1"});
            var Q31;
            Q31=makeQuery(id+"F9.opPattern","COPY",BODY,{"derivedFrom":makeQuery(id+"F8.opExtrude","SWEPT_BODY",BODY,{"disambiguationData":[OSD([sQuery(id+"F7.wireOp",EDGE,"E9"),sQuery(id+"F7.wireOp",EDGE,"E10")])]}),"instanceName":"1"});
            var Q32;
            Q32=makeQuery(id+"F9.opPattern","COPY",BODY,{"derivedFrom":makeQuery(id+"F8.opExtrude","SWEPT_BODY",BODY,{"disambiguationData":[OSD([sQuery(id+"F7.wireOp",EDGE,"E27"),sQuery(id+"F7.wireOp",EDGE,"E28"),sQuery(id+"F7.wireOp",EDGE,"E29"),sQuery(id+"F7.wireOp",EDGE,"E30"),sQuery(id+"F7.wireOp",EDGE,"E31"),sQuery(id+"F7.wireOp",EDGE,"E32"),sQuery(id+"F7.wireOp",EDGE,"E33"),sQuery(id+"F7.wireOp",EDGE,"E34"),sQuery(id+"F7.wireOp",EDGE,"E35")])]}),"instanceName":"1"});
            var Q33;
            Q33=makeQuery(id+"F9.opPattern","COPY",BODY,{"derivedFrom":makeQuery(id+"F8.opExtrude","SWEPT_BODY",BODY,{"disambiguationData":[OSD([sQuery(id+"F7.wireOp",EDGE,"E36"),sQuery(id+"F7.wireOp",EDGE,"E37")])]}),"instanceName":"1"});
            var Q34;
            Q34=makeQuery(id+"F9.opPattern","COPY",BODY,{"derivedFrom":makeQuery(id+"F8.opExtrude","SWEPT_BODY",BODY,{"disambiguationData":[OSD([sQuery(id+"F7.wireOp",EDGE,"E50"),sQuery(id+"F7.wireOp",EDGE,"E51"),sQuery(id+"F7.wireOp",EDGE,"E52"),sQuery(id+"F7.wireOp",EDGE,"E53")])]}),"instanceName":"1"});
            var Q35;
            Q35=makeQuery(id+"F9.opPattern","COPY",BODY,{"derivedFrom":makeQuery(id+"F8.opExtrude","SWEPT_BODY",BODY,{"disambiguationData":[OSD([sQuery(id+"F7.wireOp",EDGE,"E57"),sQuery(id+"F7.wireOp",EDGE,"E58"),sQuery(id+"F7.wireOp",EDGE,"E59")])]}),"instanceName":"1"});
            var Q36;
            Q36=makeQuery(id+"F9.opPattern","COPY",BODY,{"derivedFrom":makeQuery(id+"F8.opExtrude","SWEPT_BODY",BODY,{"disambiguationData":[OSD([sQuery(id+"F7.wireOp",EDGE,"E63"),sQuery(id+"F7.wireOp",EDGE,"E64"),sQuery(id+"F7.wireOp",EDGE,"E65"),sQuery(id+"F7.wireOp",EDGE,"E66")])]}),"instanceName":"1"});
            var Q37;
            Q37=makeQuery(id+"F9.opPattern","COPY",BODY,{"derivedFrom":makeQuery(id+"F8.opExtrude","SWEPT_BODY",BODY,{"disambiguationData":[OSD([sQuery(id+"F7.wireOp",EDGE,"E67"),sQuery(id+"F7.wireOp",EDGE,"E68"),sQuery(id+"F7.wireOp",EDGE,"E69"),sQuery(id+"F7.wireOp",EDGE,"E70")])]}),"instanceName":"1"});
            var Q38;
            Q38=makeQuery(id+"F9.opPattern","COPY",BODY,{"derivedFrom":makeQuery(id+"F5.opSweep","SWEPT_BODY",BODY,{"disambiguationData":[OSD([sQuery(id+"F0.wireOp",EDGE,"E0"),sQuery(id+"F2.wireOp",EDGE,"E4")])]}),"instanceName":"2"});
            var Q39;
            Q39=makeQuery(id+"F9.opPattern","COPY",BODY,{"derivedFrom":makeQuery(id+"F8.opExtrude","SWEPT_BODY",BODY,{"disambiguationData":[OSD([sQuery(id+"F7.wireOp",EDGE,"E9"),sQuery(id+"F7.wireOp",EDGE,"E10")])]}),"instanceName":"2"});
            var Q40;
            Q40=makeQuery(id+"F9.opPattern","COPY",BODY,{"derivedFrom":makeQuery(id+"F8.opExtrude","SWEPT_BODY",BODY,{"disambiguationData":[OSD([sQuery(id+"F7.wireOp",EDGE,"E21"),sQuery(id+"F7.wireOp",EDGE,"E22")])]}),"instanceName":"1"});
            var Q41;
            Q41=makeQuery(id+"F9.opPattern","COPY",BODY,{"derivedFrom":makeQuery(id+"F8.opExtrude","SWEPT_BODY",BODY,{"disambiguationData":[OSD([sQuery(id+"F7.wireOp",EDGE,"E54"),sQuery(id+"F7.wireOp",EDGE,"E55"),sQuery(id+"F7.wireOp",EDGE,"E56")])]}),"instanceName":"1"});
            var Q42;
            Q42=makeQuery(id+"F9.opPattern","COPY",BODY,{"derivedFrom":makeQuery(id+"F8.opExtrude","SWEPT_BODY",BODY,{"disambiguationData":[OSD([sQuery(id+"F7.wireOp",EDGE,"E60"),sQuery(id+"F7.wireOp",EDGE,"E61"),sQuery(id+"F7.wireOp",EDGE,"E62"),sQuery(id+"F7.wireOp",EDGE,"E71"),sQuery(id+"F7.wireOp",EDGE,"E72")])]}),"instanceName":"1"});
            var Q43;
            Q43=makeQuery(id+"F9.opPattern","COPY",BODY,{"derivedFrom":makeQuery(id+"F8.opExtrude","SWEPT_BODY",BODY,{"disambiguationData":[OSD([sQuery(id+"F7.wireOp",EDGE,"E7"),sQuery(id+"F7.wireOp",EDGE,"E8")])]}),"instanceName":"2"});
            var Q44;
            Q44=makeQuery(id+"F9.opPattern","COPY",BODY,{"derivedFrom":makeQuery(id+"F8.opExtrude","SWEPT_BODY",BODY,{"disambiguationData":[OSD([sQuery(id+"F7.wireOp",EDGE,"E11"),sQuery(id+"F7.wireOp",EDGE,"E12")])]}),"instanceName":"2"});
            var Q45;
            Q45=makeQuery(id+"F9.opPattern","COPY",BODY,{"derivedFrom":makeQuery(id+"F8.opExtrude","SWEPT_BODY",BODY,{"disambiguationData":[OSD([sQuery(id+"F7.wireOp",EDGE,"E13"),sQuery(id+"F7.wireOp",EDGE,"E14"),sQuery(id+"F7.wireOp",EDGE,"E15"),sQuery(id+"F7.wireOp",EDGE,"E16"),sQuery(id+"F7.wireOp",EDGE,"E17"),sQuery(id+"F7.wireOp",EDGE,"E18"),sQuery(id+"F7.wireOp",EDGE,"E19"),sQuery(id+"F7.wireOp",EDGE,"E20")])]}),"instanceName":"2"});
            var Q46;
            Q46=makeQuery(id+"F9.opPattern","COPY",BODY,{"derivedFrom":makeQuery(id+"F8.opExtrude","SWEPT_BODY",BODY,{"disambiguationData":[OSD([sQuery(id+"F7.wireOp",EDGE,"E21"),sQuery(id+"F7.wireOp",EDGE,"E22")])]}),"instanceName":"2"});
            var Q47;
            Q47=makeQuery(id+"F9.opPattern","COPY",BODY,{"derivedFrom":makeQuery(id+"F8.opExtrude","SWEPT_BODY",BODY,{"disambiguationData":[OSD([sQuery(id+"F7.wireOp",EDGE,"E23"),sQuery(id+"F7.wireOp",EDGE,"E24")])]}),"instanceName":"2"});
            var Q48;
            Q48=makeQuery(id+"F9.opPattern","COPY",BODY,{"derivedFrom":makeQuery(id+"F8.opExtrude","SWEPT_BODY",BODY,{"disambiguationData":[OSD([sQuery(id+"F7.wireOp",EDGE,"E27"),sQuery(id+"F7.wireOp",EDGE,"E28"),sQuery(id+"F7.wireOp",EDGE,"E29"),sQuery(id+"F7.wireOp",EDGE,"E30"),sQuery(id+"F7.wireOp",EDGE,"E31"),sQuery(id+"F7.wireOp",EDGE,"E32"),sQuery(id+"F7.wireOp",EDGE,"E33"),sQuery(id+"F7.wireOp",EDGE,"E34"),sQuery(id+"F7.wireOp",EDGE,"E35")])]}),"instanceName":"2"});
            var Q49;
            Q49=makeQuery(id+"F9.opPattern","COPY",BODY,{"derivedFrom":makeQuery(id+"F8.opExtrude","SWEPT_BODY",BODY,{"disambiguationData":[OSD([sQuery(id+"F7.wireOp",EDGE,"E36"),sQuery(id+"F7.wireOp",EDGE,"E37")])]}),"instanceName":"2"});
            var Q50;
            Q50=makeQuery(id+"F9.opPattern","COPY",BODY,{"derivedFrom":makeQuery(id+"F8.opExtrude","SWEPT_BODY",BODY,{"disambiguationData":[OSD([sQuery(id+"F7.wireOp",EDGE,"E38"),sQuery(id+"F7.wireOp",EDGE,"E39")])]}),"instanceName":"2"});
            var Q51;
            Q51=makeQuery(id+"F9.opPattern","COPY",BODY,{"derivedFrom":makeQuery(id+"F8.opExtrude","SWEPT_BODY",BODY,{"disambiguationData":[OSD([sQuery(id+"F7.wireOp",EDGE,"E40"),sQuery(id+"F7.wireOp",EDGE,"E41")])]}),"instanceName":"2"});
            var Q52;
            Q52=makeQuery(id+"F9.opPattern","COPY",BODY,{"derivedFrom":makeQuery(id+"F8.opExtrude","SWEPT_BODY",BODY,{"disambiguationData":[OSD([sQuery(id+"F7.wireOp",EDGE,"E73"),sQuery(id+"F7.wireOp",EDGE,"E74.0"),sQuery(id+"F7.wireOp",EDGE,"E75"),sQuery(id+"F7.wireOp",EDGE,"E76")])]}),"instanceName":"1"});
            var Q53;
            Q53=makeQuery(id+"F9.opPattern","COPY",BODY,{"derivedFrom":makeQuery(id+"F8.opExtrude","SWEPT_BODY",BODY,{"disambiguationData":[OSD([sQuery(id+"F7.wireOp",EDGE,"E25"),sQuery(id+"F7.wireOp",EDGE,"E26")])]}),"instanceName":"2"});
            var Q54;
            Q54=makeQuery(id+"F9.opPattern","COPY",BODY,{"derivedFrom":makeQuery(id+"F8.opExtrude","SWEPT_BODY",BODY,{"disambiguationData":[OSD([sQuery(id+"F7.wireOp",EDGE,"E42"),sQuery(id+"F7.wireOp",EDGE,"E43"),sQuery(id+"F7.wireOp",EDGE,"E44"),sQuery(id+"F7.wireOp",EDGE,"E45"),sQuery(id+"F7.wireOp",EDGE,"E46"),sQuery(id+"F7.wireOp",EDGE,"E47"),sQuery(id+"F7.wireOp",EDGE,"E48"),sQuery(id+"F7.wireOp",EDGE,"E49")])]}),"instanceName":"2"});
            var Q55;
            Q55=makeQuery(id+"F9.opPattern","COPY",BODY,{"derivedFrom":makeQuery(id+"F8.opExtrude","SWEPT_BODY",BODY,{"disambiguationData":[OSD([sQuery(id+"F7.wireOp",EDGE,"E50"),sQuery(id+"F7.wireOp",EDGE,"E51"),sQuery(id+"F7.wireOp",EDGE,"E52"),sQuery(id+"F7.wireOp",EDGE,"E53")])]}),"instanceName":"2"});
            var Q56;
            Q56=makeQuery(id+"F9.opPattern","COPY",BODY,{"derivedFrom":makeQuery(id+"F8.opExtrude","SWEPT_BODY",BODY,{"disambiguationData":[OSD([sQuery(id+"F7.wireOp",EDGE,"E54"),sQuery(id+"F7.wireOp",EDGE,"E55"),sQuery(id+"F7.wireOp",EDGE,"E56")])]}),"instanceName":"2"});
            var Q57;
            Q57=makeQuery(id+"F9.opPattern","COPY",BODY,{"derivedFrom":makeQuery(id+"F8.opExtrude","SWEPT_BODY",BODY,{"disambiguationData":[OSD([sQuery(id+"F7.wireOp",EDGE,"E57"),sQuery(id+"F7.wireOp",EDGE,"E58"),sQuery(id+"F7.wireOp",EDGE,"E59")])]}),"instanceName":"2"});
            var Q58;
            Q58=makeQuery(id+"F9.opPattern","COPY",BODY,{"derivedFrom":makeQuery(id+"F8.opExtrude","SWEPT_BODY",BODY,{"disambiguationData":[OSD([sQuery(id+"F7.wireOp",EDGE,"E63"),sQuery(id+"F7.wireOp",EDGE,"E64"),sQuery(id+"F7.wireOp",EDGE,"E65"),sQuery(id+"F7.wireOp",EDGE,"E66")])]}),"instanceName":"2"});
            var Q59;
            Q59=makeQuery(id+"F9.opPattern","COPY",BODY,{"derivedFrom":makeQuery(id+"F8.opExtrude","SWEPT_BODY",BODY,{"disambiguationData":[OSD([sQuery(id+"F7.wireOp",EDGE,"E73"),sQuery(id+"F7.wireOp",EDGE,"E74.0"),sQuery(id+"F7.wireOp",EDGE,"E75"),sQuery(id+"F7.wireOp",EDGE,"E76")])]}),"instanceName":"2"});
            var Q60;
            Q60=makeQuery(id+"F9.opPattern","COPY",BODY,{"derivedFrom":makeQuery(id+"F5.opSweep","SWEPT_BODY",BODY,{"disambiguationData":[OSD([sQuery(id+"F0.wireOp",EDGE,"E0"),sQuery(id+"F2.wireOp",EDGE,"E4")])]}),"instanceName":"3"});
            var Q61;
            Q61=makeQuery(id+"F9.opPattern","COPY",BODY,{"derivedFrom":makeQuery(id+"F8.opExtrude","SWEPT_BODY",BODY,{"disambiguationData":[OSD([sQuery(id+"F7.wireOp",EDGE,"E7"),sQuery(id+"F7.wireOp",EDGE,"E8")])]}),"instanceName":"3"});
            var Q62;
            Q62=makeQuery(id+"F9.opPattern","COPY",BODY,{"derivedFrom":makeQuery(id+"F8.opExtrude","SWEPT_BODY",BODY,{"disambiguationData":[OSD([sQuery(id+"F7.wireOp",EDGE,"E60"),sQuery(id+"F7.wireOp",EDGE,"E61"),sQuery(id+"F7.wireOp",EDGE,"E62"),sQuery(id+"F7.wireOp",EDGE,"E71"),sQuery(id+"F7.wireOp",EDGE,"E72")])]}),"instanceName":"2"});
            var Q63;
            Q63=makeQuery(id+"F9.opPattern","COPY",BODY,{"derivedFrom":makeQuery(id+"F8.opExtrude","SWEPT_BODY",BODY,{"disambiguationData":[OSD([sQuery(id+"F7.wireOp",EDGE,"E67"),sQuery(id+"F7.wireOp",EDGE,"E68"),sQuery(id+"F7.wireOp",EDGE,"E69"),sQuery(id+"F7.wireOp",EDGE,"E70")])]}),"instanceName":"2"});
            var Q64;
            Q64=makeQuery(id+"F9.opPattern","COPY",BODY,{"derivedFrom":makeQuery(id+"F8.opExtrude","SWEPT_BODY",BODY,{"disambiguationData":[OSD([sQuery(id+"F7.wireOp",EDGE,"E9"),sQuery(id+"F7.wireOp",EDGE,"E10")])]}),"instanceName":"3"});
            var Q65;
            Q65=makeQuery(id+"F9.opPattern","COPY",BODY,{"derivedFrom":makeQuery(id+"F8.opExtrude","SWEPT_BODY",BODY,{"disambiguationData":[OSD([sQuery(id+"F7.wireOp",EDGE,"E11"),sQuery(id+"F7.wireOp",EDGE,"E12")])]}),"instanceName":"3"});
            var Q66;
            Q66=makeQuery(id+"F9.opPattern","COPY",BODY,{"derivedFrom":makeQuery(id+"F8.opExtrude","SWEPT_BODY",BODY,{"disambiguationData":[OSD([sQuery(id+"F7.wireOp",EDGE,"E13"),sQuery(id+"F7.wireOp",EDGE,"E14"),sQuery(id+"F7.wireOp",EDGE,"E15"),sQuery(id+"F7.wireOp",EDGE,"E16"),sQuery(id+"F7.wireOp",EDGE,"E17"),sQuery(id+"F7.wireOp",EDGE,"E18"),sQuery(id+"F7.wireOp",EDGE,"E19"),sQuery(id+"F7.wireOp",EDGE,"E20")])]}),"instanceName":"3"});
            var Q67;
            Q67=makeQuery(id+"F9.opPattern","COPY",BODY,{"derivedFrom":makeQuery(id+"F8.opExtrude","SWEPT_BODY",BODY,{"disambiguationData":[OSD([sQuery(id+"F7.wireOp",EDGE,"E21"),sQuery(id+"F7.wireOp",EDGE,"E22")])]}),"instanceName":"3"});
            var Q68;
            Q68=makeQuery(id+"F9.opPattern","COPY",BODY,{"derivedFrom":makeQuery(id+"F8.opExtrude","SWEPT_BODY",BODY,{"disambiguationData":[OSD([sQuery(id+"F7.wireOp",EDGE,"E23"),sQuery(id+"F7.wireOp",EDGE,"E24")])]}),"instanceName":"3"});
            var Q69;
            Q69=makeQuery(id+"F9.opPattern","COPY",BODY,{"derivedFrom":makeQuery(id+"F8.opExtrude","SWEPT_BODY",BODY,{"disambiguationData":[OSD([sQuery(id+"F7.wireOp",EDGE,"E25"),sQuery(id+"F7.wireOp",EDGE,"E26")])]}),"instanceName":"3"});
            var Q70;
            Q70=makeQuery(id+"F9.opPattern","COPY",BODY,{"derivedFrom":makeQuery(id+"F8.opExtrude","SWEPT_BODY",BODY,{"disambiguationData":[OSD([sQuery(id+"F7.wireOp",EDGE,"E36"),sQuery(id+"F7.wireOp",EDGE,"E37")])]}),"instanceName":"3"});
            var Q71;
            Q71=makeQuery(id+"F9.opPattern","COPY",BODY,{"derivedFrom":makeQuery(id+"F8.opExtrude","SWEPT_BODY",BODY,{"disambiguationData":[OSD([sQuery(id+"F7.wireOp",EDGE,"E38"),sQuery(id+"F7.wireOp",EDGE,"E39")])]}),"instanceName":"3"});
            var Q72;
            Q72=makeQuery(id+"F9.opPattern","COPY",BODY,{"derivedFrom":makeQuery(id+"F8.opExtrude","SWEPT_BODY",BODY,{"disambiguationData":[OSD([sQuery(id+"F7.wireOp",EDGE,"E40"),sQuery(id+"F7.wireOp",EDGE,"E41")])]}),"instanceName":"3"});
            var Q73;
            Q73=makeQuery(id+"F9.opPattern","COPY",BODY,{"derivedFrom":makeQuery(id+"F8.opExtrude","SWEPT_BODY",BODY,{"disambiguationData":[OSD([sQuery(id+"F7.wireOp",EDGE,"E42"),sQuery(id+"F7.wireOp",EDGE,"E43"),sQuery(id+"F7.wireOp",EDGE,"E44"),sQuery(id+"F7.wireOp",EDGE,"E45"),sQuery(id+"F7.wireOp",EDGE,"E46"),sQuery(id+"F7.wireOp",EDGE,"E47"),sQuery(id+"F7.wireOp",EDGE,"E48"),sQuery(id+"F7.wireOp",EDGE,"E49")])]}),"instanceName":"3"});
            var Q74;
            Q74=makeQuery(id+"F9.opPattern","COPY",BODY,{"derivedFrom":makeQuery(id+"F8.opExtrude","SWEPT_BODY",BODY,{"disambiguationData":[OSD([sQuery(id+"F7.wireOp",EDGE,"E27"),sQuery(id+"F7.wireOp",EDGE,"E28"),sQuery(id+"F7.wireOp",EDGE,"E29"),sQuery(id+"F7.wireOp",EDGE,"E30"),sQuery(id+"F7.wireOp",EDGE,"E31"),sQuery(id+"F7.wireOp",EDGE,"E32"),sQuery(id+"F7.wireOp",EDGE,"E33"),sQuery(id+"F7.wireOp",EDGE,"E34"),sQuery(id+"F7.wireOp",EDGE,"E35")])]}),"instanceName":"3"});
            var Q75;
            Q75=makeQuery(id+"F9.opPattern","COPY",BODY,{"derivedFrom":makeQuery(id+"F8.opExtrude","SWEPT_BODY",BODY,{"disambiguationData":[OSD([sQuery(id+"F7.wireOp",EDGE,"E50"),sQuery(id+"F7.wireOp",EDGE,"E51"),sQuery(id+"F7.wireOp",EDGE,"E52"),sQuery(id+"F7.wireOp",EDGE,"E53")])]}),"instanceName":"3"});
            var Q76;
            Q76=makeQuery(id+"F9.opPattern","COPY",BODY,{"derivedFrom":makeQuery(id+"F8.opExtrude","SWEPT_BODY",BODY,{"disambiguationData":[OSD([sQuery(id+"F7.wireOp",EDGE,"E54"),sQuery(id+"F7.wireOp",EDGE,"E55"),sQuery(id+"F7.wireOp",EDGE,"E56")])]}),"instanceName":"3"});
            var Q77;
            Q77=makeQuery(id+"F9.opPattern","COPY",BODY,{"derivedFrom":makeQuery(id+"F8.opExtrude","SWEPT_BODY",BODY,{"disambiguationData":[OSD([sQuery(id+"F7.wireOp",EDGE,"E57"),sQuery(id+"F7.wireOp",EDGE,"E58"),sQuery(id+"F7.wireOp",EDGE,"E59")])]}),"instanceName":"3"});
            var Q78;
            Q78=makeQuery(id+"F9.opPattern","COPY",BODY,{"derivedFrom":makeQuery(id+"F8.opExtrude","SWEPT_BODY",BODY,{"disambiguationData":[OSD([sQuery(id+"F7.wireOp",EDGE,"E60"),sQuery(id+"F7.wireOp",EDGE,"E61"),sQuery(id+"F7.wireOp",EDGE,"E62"),sQuery(id+"F7.wireOp",EDGE,"E71"),sQuery(id+"F7.wireOp",EDGE,"E72")])]}),"instanceName":"3"});
            var Q79;
            Q79=makeQuery(id+"F9.opPattern","COPY",BODY,{"derivedFrom":makeQuery(id+"F8.opExtrude","SWEPT_BODY",BODY,{"disambiguationData":[OSD([sQuery(id+"F7.wireOp",EDGE,"E63"),sQuery(id+"F7.wireOp",EDGE,"E64"),sQuery(id+"F7.wireOp",EDGE,"E65"),sQuery(id+"F7.wireOp",EDGE,"E66")])]}),"instanceName":"3"});
            var Q80;
            Q80=makeQuery(id+"F9.opPattern","COPY",BODY,{"derivedFrom":makeQuery(id+"F8.opExtrude","SWEPT_BODY",BODY,{"disambiguationData":[OSD([sQuery(id+"F7.wireOp",EDGE,"E67"),sQuery(id+"F7.wireOp",EDGE,"E68"),sQuery(id+"F7.wireOp",EDGE,"E69"),sQuery(id+"F7.wireOp",EDGE,"E70")])]}),"instanceName":"3"});
            var Q81;
            Q81=makeQuery(id+"F9.opPattern","COPY",BODY,{"derivedFrom":makeQuery(id+"F5.opSweep","SWEPT_BODY",BODY,{"disambiguationData":[OSD([sQuery(id+"F0.wireOp",EDGE,"E0"),sQuery(id+"F2.wireOp",EDGE,"E4")])]}),"instanceName":"4"});
            var Q82;
            Q82=makeQuery(id+"F9.opPattern","COPY",BODY,{"derivedFrom":makeQuery(id+"F8.opExtrude","SWEPT_BODY",BODY,{"disambiguationData":[OSD([sQuery(id+"F7.wireOp",EDGE,"E7"),sQuery(id+"F7.wireOp",EDGE,"E8")])]}),"instanceName":"4"});
            var Q83;
            Q83=makeQuery(id+"F9.opPattern","COPY",BODY,{"derivedFrom":makeQuery(id+"F8.opExtrude","SWEPT_BODY",BODY,{"disambiguationData":[OSD([sQuery(id+"F7.wireOp",EDGE,"E9"),sQuery(id+"F7.wireOp",EDGE,"E10")])]}),"instanceName":"4"});
            var Q84;
            Q84=makeQuery(id+"F9.opPattern","COPY",BODY,{"derivedFrom":makeQuery(id+"F8.opExtrude","SWEPT_BODY",BODY,{"disambiguationData":[OSD([sQuery(id+"F7.wireOp",EDGE,"E11"),sQuery(id+"F7.wireOp",EDGE,"E12")])]}),"instanceName":"4"});
            var Q85;
            Q85=makeQuery(id+"F9.opPattern","COPY",BODY,{"derivedFrom":makeQuery(id+"F8.opExtrude","SWEPT_BODY",BODY,{"disambiguationData":[OSD([sQuery(id+"F7.wireOp",EDGE,"E73"),sQuery(id+"F7.wireOp",EDGE,"E74.0"),sQuery(id+"F7.wireOp",EDGE,"E75"),sQuery(id+"F7.wireOp",EDGE,"E76")])]}),"instanceName":"3"});
            var Q86;
            Q86=makeQuery(id+"F9.opPattern","COPY",BODY,{"derivedFrom":makeQuery(id+"F8.opExtrude","SWEPT_BODY",BODY,{"disambiguationData":[OSD([sQuery(id+"F7.wireOp",EDGE,"E13"),sQuery(id+"F7.wireOp",EDGE,"E14"),sQuery(id+"F7.wireOp",EDGE,"E15"),sQuery(id+"F7.wireOp",EDGE,"E16"),sQuery(id+"F7.wireOp",EDGE,"E17"),sQuery(id+"F7.wireOp",EDGE,"E18"),sQuery(id+"F7.wireOp",EDGE,"E19"),sQuery(id+"F7.wireOp",EDGE,"E20")])]}),"instanceName":"4"});
            var Q87;
            Q87=makeQuery(id+"F9.opPattern","COPY",BODY,{"derivedFrom":makeQuery(id+"F8.opExtrude","SWEPT_BODY",BODY,{"disambiguationData":[OSD([sQuery(id+"F7.wireOp",EDGE,"E21"),sQuery(id+"F7.wireOp",EDGE,"E22")])]}),"instanceName":"4"});
            var Q88;
            Q88=makeQuery(id+"F9.opPattern","COPY",BODY,{"derivedFrom":makeQuery(id+"F8.opExtrude","SWEPT_BODY",BODY,{"disambiguationData":[OSD([sQuery(id+"F7.wireOp",EDGE,"E23"),sQuery(id+"F7.wireOp",EDGE,"E24")])]}),"instanceName":"4"});
            var Q89;
            Q89=makeQuery(id+"F9.opPattern","COPY",BODY,{"derivedFrom":makeQuery(id+"F8.opExtrude","SWEPT_BODY",BODY,{"disambiguationData":[OSD([sQuery(id+"F7.wireOp",EDGE,"E25"),sQuery(id+"F7.wireOp",EDGE,"E26")])]}),"instanceName":"4"});
            var Q90;
            Q90=makeQuery(id+"F9.opPattern","COPY",BODY,{"derivedFrom":makeQuery(id+"F8.opExtrude","SWEPT_BODY",BODY,{"disambiguationData":[OSD([sQuery(id+"F7.wireOp",EDGE,"E27"),sQuery(id+"F7.wireOp",EDGE,"E28"),sQuery(id+"F7.wireOp",EDGE,"E29"),sQuery(id+"F7.wireOp",EDGE,"E30"),sQuery(id+"F7.wireOp",EDGE,"E31"),sQuery(id+"F7.wireOp",EDGE,"E32"),sQuery(id+"F7.wireOp",EDGE,"E33"),sQuery(id+"F7.wireOp",EDGE,"E34"),sQuery(id+"F7.wireOp",EDGE,"E35")])]}),"instanceName":"4"});
            var Q91;
            Q91=makeQuery(id+"F9.opPattern","COPY",BODY,{"derivedFrom":makeQuery(id+"F8.opExtrude","SWEPT_BODY",BODY,{"disambiguationData":[OSD([sQuery(id+"F7.wireOp",EDGE,"E36"),sQuery(id+"F7.wireOp",EDGE,"E37")])]}),"instanceName":"4"});
            var Q92;
            Q92=makeQuery(id+"F9.opPattern","COPY",BODY,{"derivedFrom":makeQuery(id+"F8.opExtrude","SWEPT_BODY",BODY,{"disambiguationData":[OSD([sQuery(id+"F7.wireOp",EDGE,"E38"),sQuery(id+"F7.wireOp",EDGE,"E39")])]}),"instanceName":"4"});
            var Q93;
            Q93=makeQuery(id+"F9.opPattern","COPY",BODY,{"derivedFrom":makeQuery(id+"F8.opExtrude","SWEPT_BODY",BODY,{"disambiguationData":[OSD([sQuery(id+"F7.wireOp",EDGE,"E40"),sQuery(id+"F7.wireOp",EDGE,"E41")])]}),"instanceName":"4"});
            var Q94;
            Q94=makeQuery(id+"F9.opPattern","COPY",BODY,{"derivedFrom":makeQuery(id+"F8.opExtrude","SWEPT_BODY",BODY,{"disambiguationData":[OSD([sQuery(id+"F7.wireOp",EDGE,"E50"),sQuery(id+"F7.wireOp",EDGE,"E51"),sQuery(id+"F7.wireOp",EDGE,"E52"),sQuery(id+"F7.wireOp",EDGE,"E53")])]}),"instanceName":"4"});
            var Q95;
            Q95=makeQuery(id+"F9.opPattern","COPY",BODY,{"derivedFrom":makeQuery(id+"F8.opExtrude","SWEPT_BODY",BODY,{"disambiguationData":[OSD([sQuery(id+"F7.wireOp",EDGE,"E54"),sQuery(id+"F7.wireOp",EDGE,"E55"),sQuery(id+"F7.wireOp",EDGE,"E56")])]}),"instanceName":"4"});
            var Q96;
            Q96=makeQuery(id+"F9.opPattern","COPY",BODY,{"derivedFrom":makeQuery(id+"F8.opExtrude","SWEPT_BODY",BODY,{"disambiguationData":[OSD([sQuery(id+"F7.wireOp",EDGE,"E57"),sQuery(id+"F7.wireOp",EDGE,"E58"),sQuery(id+"F7.wireOp",EDGE,"E59")])]}),"instanceName":"4"});
            var Q97;
            Q97=makeQuery(id+"F1.opExtrude","SWEPT_BODY",BODY,{"disambiguationData":[OSD([sQuery(id+"F0.wireOp",EDGE,"E1"),sQuery(id+"F0.wireOp",EDGE,"E2"),sQuery(id+"F0.wireOp",EDGE,"E0")])]});
            booleanBodies(context, id + "F11", {"operationType" : BooleanOperationType.SUBTRACTION, "tools" : qUnion([Q0, Q1, Q2, Q3, Q4, Q5, Q6, Q7, Q8, Q9, Q10, Q11, Q12, Q13, Q14, Q15, Q16, Q17, Q18, Q19, Q20, Q21, Q22, Q23, Q24, Q25, Q26, Q27, Q28, Q29, Q30, Q31, Q32, Q33, Q34, Q35, Q36, Q37, Q38, Q39, Q40, Q41, Q42, Q43, Q44, Q45, Q46, Q47, Q48, Q49, Q50, Q51, Q52, Q53, Q54, Q55, Q56, Q57, Q58, Q59, Q60, Q61, Q62, Q63, Q64, Q65, Q66, Q67, Q68, Q69, Q70, Q71, Q72, Q73, Q74, Q75, Q76, Q77, Q78, Q79, Q80, Q81, Q82, Q83, Q84, Q85, Q86, Q87, Q88, Q89, Q90, Q91, Q92, Q93, Q94, Q95, Q96]), "targets" : qUnion([Q97])});
        }
    });
